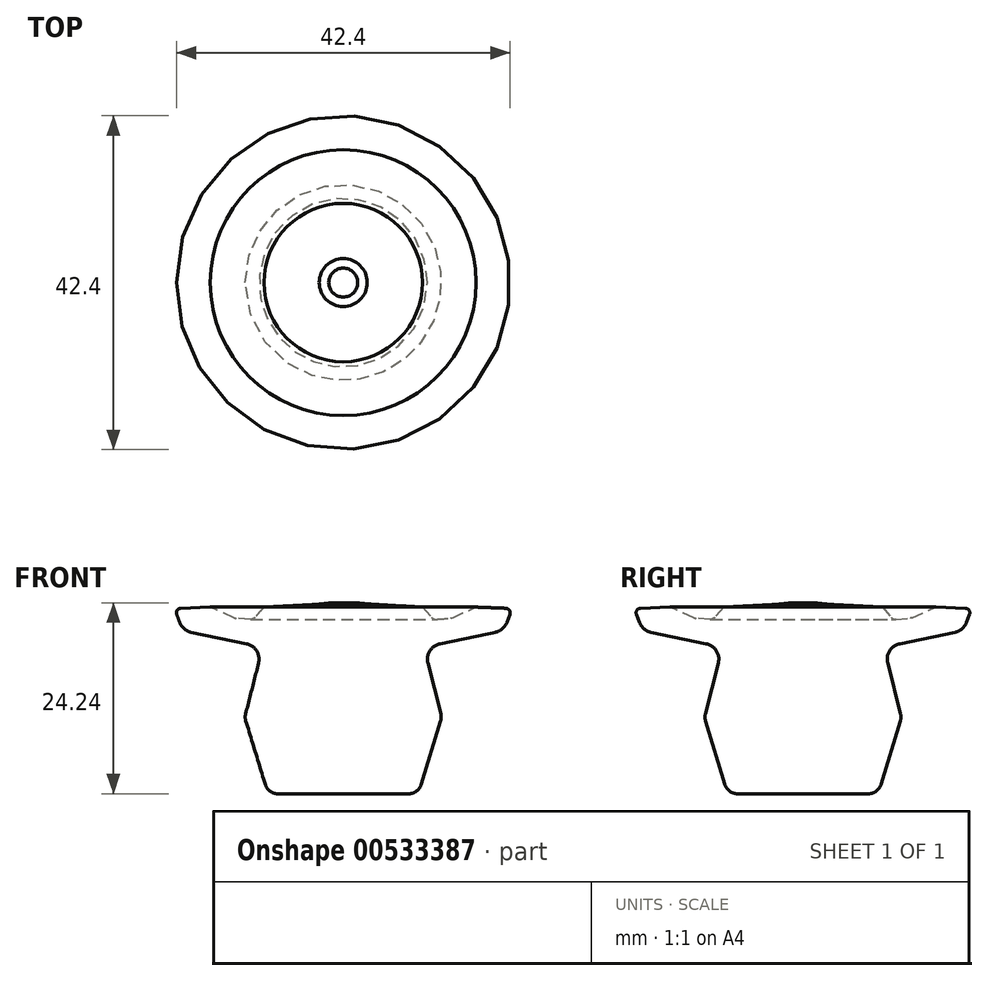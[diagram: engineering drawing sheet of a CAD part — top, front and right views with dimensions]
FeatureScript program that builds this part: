
annotation { "Feature Type Name" : "Feature", "Feature Type Description" : "" }
export const myFeature = defineFeature(function(context is Context, id is Id, definition is map)
    precondition{}
    {
        {
            var Q0;
            Q0=qCreatedBy(makeId("Front.planeOp"),FACE);
            var sketch = newSketch(context, id + "F0", { "sketchPlane" : qUnion([Q0])});
            skLineSegment(sketch, "E0", {"start": v(0, 0) * mm, "end": v(-9.54, 0) * mm});
            skLineSegment(sketch, "E1", {"start": v(-9.54, 0) * mm, "end": v(-12.51, 9.71) * mm});
            skLineSegment(sketch, "E2", {"start": v(-12.51, 9.71) * mm, "end": v(-10.24, 18.64) * mm});
            skLineSegment(sketch, "E3", {"start": v(-10.24, 18.64) * mm, "end": v(-20.39, 20.74) * mm});
            skLineSegment(sketch, "E4", {"start": v(-20.39, 20.74) * mm, "end": v(-21.44, 23.54) * mm});
            skLineSegment(sketch, "E5", {"start": v(-21.44, 23.54) * mm, "end": v(-16.89, 23.71) * mm});
            skLineSegment(sketch, "E6", {"start": v(-16.89, 23.71) * mm, "end": v(-13.74, 22.31) * mm});
            skLineSegment(sketch, "E7", {"start": v(-13.74, 22.31) * mm, "end": v(-11.46, 22.14) * mm});
            skLineSegment(sketch, "E8", {"start": v(-11.46, 22.14) * mm, "end": v(-10.06, 23.71) * mm});
            skLineSegment(sketch, "E9", {"start": v(-10.06, 23.71) * mm, "end": v(-3.94, 24.06) * mm});
            skLineSegment(sketch, "E10", {"start": v(-3.94, 24.06) * mm, "end": v(-3.04, 24.12) * mm});
            skLineSegment(sketch, "E11", {"start": v(-3.04, 24.12) * mm, "end": v(-1.84, 24.24) * mm});
            skLineSegment(sketch, "E12", {"start": v(-1.84, 24.24) * mm, "end": v(0, 24.24) * mm});
            skLineSegment(sketch, "E13", {"start": v(0, 24.24) * mm, "end": v(0, 0) * mm});
            skSolve(sketch);
        }
        {
            var Q0;
            Q0=makeQuery(id+"F0.imprint","IMPRINT",FACE,{"disambiguationData":[TD([[makeQuery(id+"F0.imprint","IMPRINT",EDGE,{"derivedFrom":sQuery(id+"F0.wireOp",EDGE,"E0")}),-1.0]])]});
            var Q1;
            Q1=sQuery(id+"F0.wireOp",EDGE,"E13");
            revolve(context, id + "F1", {"entities" : qUnion([Q0]), "axis" : qUnion([Q1]), "revolveType" : RevolveType.FULL});
        }
        {
            var Q0;
            Q0=makeQuery(id+"F1.opRevolve","SWEPT_EDGE",EDGE,{"disambiguationData":[OSD([sQuery(id+"F0.wireOp",EDGE,"E4"),sQuery(id+"F0.wireOp",EDGE,"E5")])]});
            fillet(context, id + "F2", {"entities" : qUnion([Q0]), "radius" : 0.56 * mm, "tangentPropagation" : true, "allowEdgeOverflow" : false});
        }
        {
            var Q0;
            Q0=makeQuery(id+"F1.opRevolve","SWEPT_FACE",FACE,{"disambiguationData":[OSD([sQuery(id+"F0.wireOp",EDGE,"E3")])]});
            fillet(context, id + "F3", {"entities" : qUnion([Q0]), "radius" : 2 * mm, "tangentPropagation" : true, "allowEdgeOverflow" : false});
        }
        {
            var Q0;
            Q0=makeQuery(id+"F1.opRevolve","SWEPT_FACE",FACE,{"disambiguationData":[OSD([sQuery(id+"F0.wireOp",EDGE,"E7")])]});
            fillet(context, id + "F4", {"entities" : qUnion([Q0]), "radius" : 0.68 * mm, "tangentPropagation" : true, "allowEdgeOverflow" : false});
        }
        {
            var Q0;
            Q0=makeQuery(id+"F1.opRevolve","SWEPT_FACE",FACE,{"disambiguationData":[OSD([sQuery(id+"F0.wireOp",EDGE,"E1")])]});
            fillet(context, id + "F5", {"entities" : qUnion([Q0]), "radius" : 1.64 * mm, "tangentPropagation" : true, "allowEdgeOverflow" : false});
        }
    });
